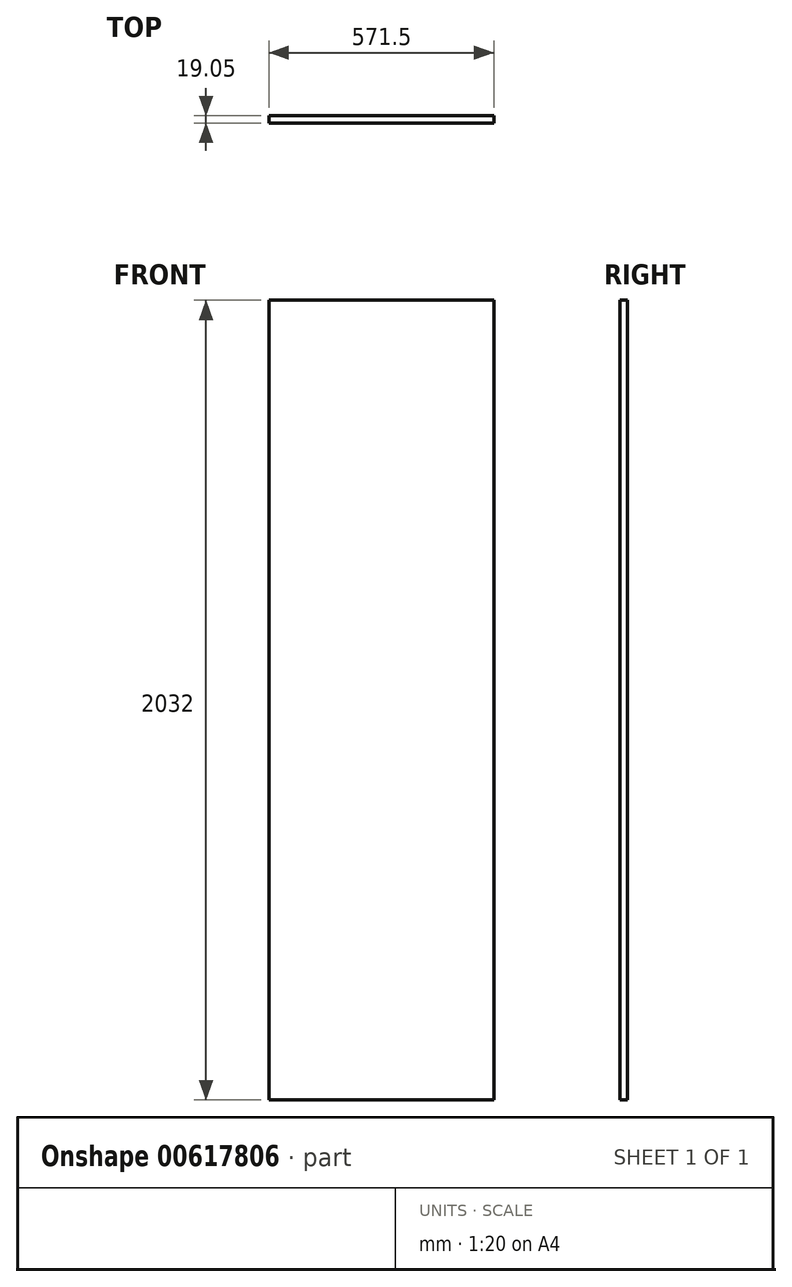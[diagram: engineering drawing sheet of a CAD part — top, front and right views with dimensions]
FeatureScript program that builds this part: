
annotation { "Feature Type Name" : "Feature", "Feature Type Description" : "" }
export const myFeature = defineFeature(function(context is Context, id is Id, definition is map)
    precondition{}
    {
        {
            var Q0;
            Q0=qCreatedBy(makeId("Front.planeOp"),FACE);
            var sketch = newSketch(context, id + "F0", { "sketchPlane" : qUnion([Q0])});
            skLineSegment(sketch, "E0.bottom", {"start": v(285.75, 1016) * mm, "end": v(-285.75, 1016) * mm});
            skLineSegment(sketch, "E0.top", {"start": v(285.75, -1016) * mm, "end": v(-285.75, -1016) * mm});
            skLineSegment(sketch, "E0.left", {"start": v(285.75, 1016) * mm, "end": v(285.75, -1016) * mm});
            skLineSegment(sketch, "E0.right", {"start": v(-285.75, 1016) * mm, "end": v(-285.75, -1016) * mm});
            skPoint(sketch, "E0.middle", {"position": v(0, 0) * mm});
            skSolve(sketch);
        }
        {
            var Q0;
            Q0=makeQuery(id+"F0.imprint","IMPRINT",FACE,{"disambiguationData":[TD([[makeQuery(id+"F0.imprint","IMPRINT",EDGE,{"derivedFrom":sQuery(id+"F0.wireOp",EDGE,"E0.bottom")}),1.0]])]});
            extrude(context, id + "F1", {"entities" : qUnion([Q0]), "depth" : 19.05 * mm, "offsetDistance" : 25.4 * mm});
        }
    });
